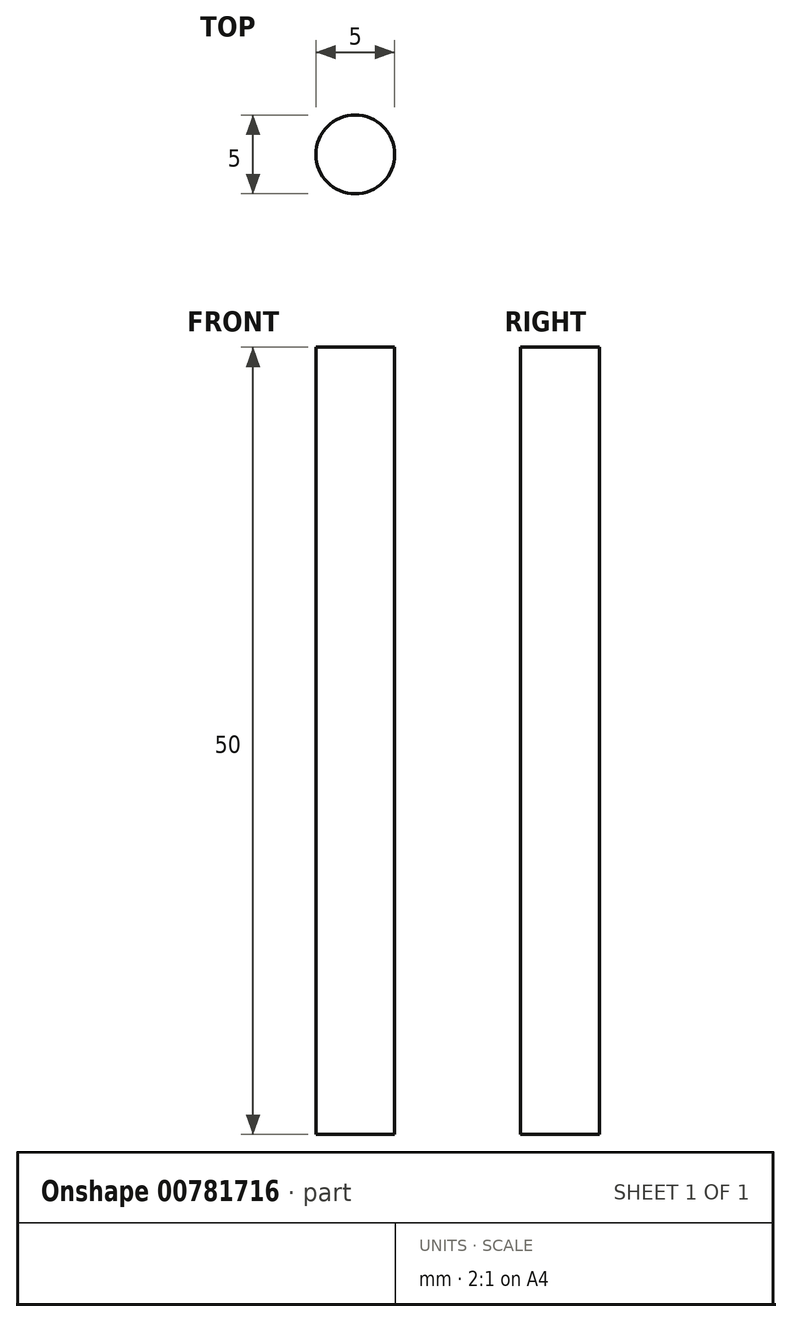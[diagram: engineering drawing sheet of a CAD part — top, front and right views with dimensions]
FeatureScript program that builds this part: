
annotation { "Feature Type Name" : "Feature", "Feature Type Description" : "" }
export const myFeature = defineFeature(function(context is Context, id is Id, definition is map)
    precondition{}
    {
        {
            var Q0;
            Q0=qCreatedBy(makeId("Top.planeOp"),FACE);
            var sketch = newSketch(context, id + "F0", { "sketchPlane" : qUnion([Q0])});
            skCircle(sketch, "E0", {"center": v(0, 0) * mm, "radius": 2.5 * mm});
            skSolve(sketch);
        }
        {
            var Q0;
            Q0 = qSketchRegion(id + "F0", true);
            extrude(context, id + "F1", {"entities" : qUnion([Q0]), "depth" : 50 * mm, "offsetDistance" : 25 * mm});
        }
    });
